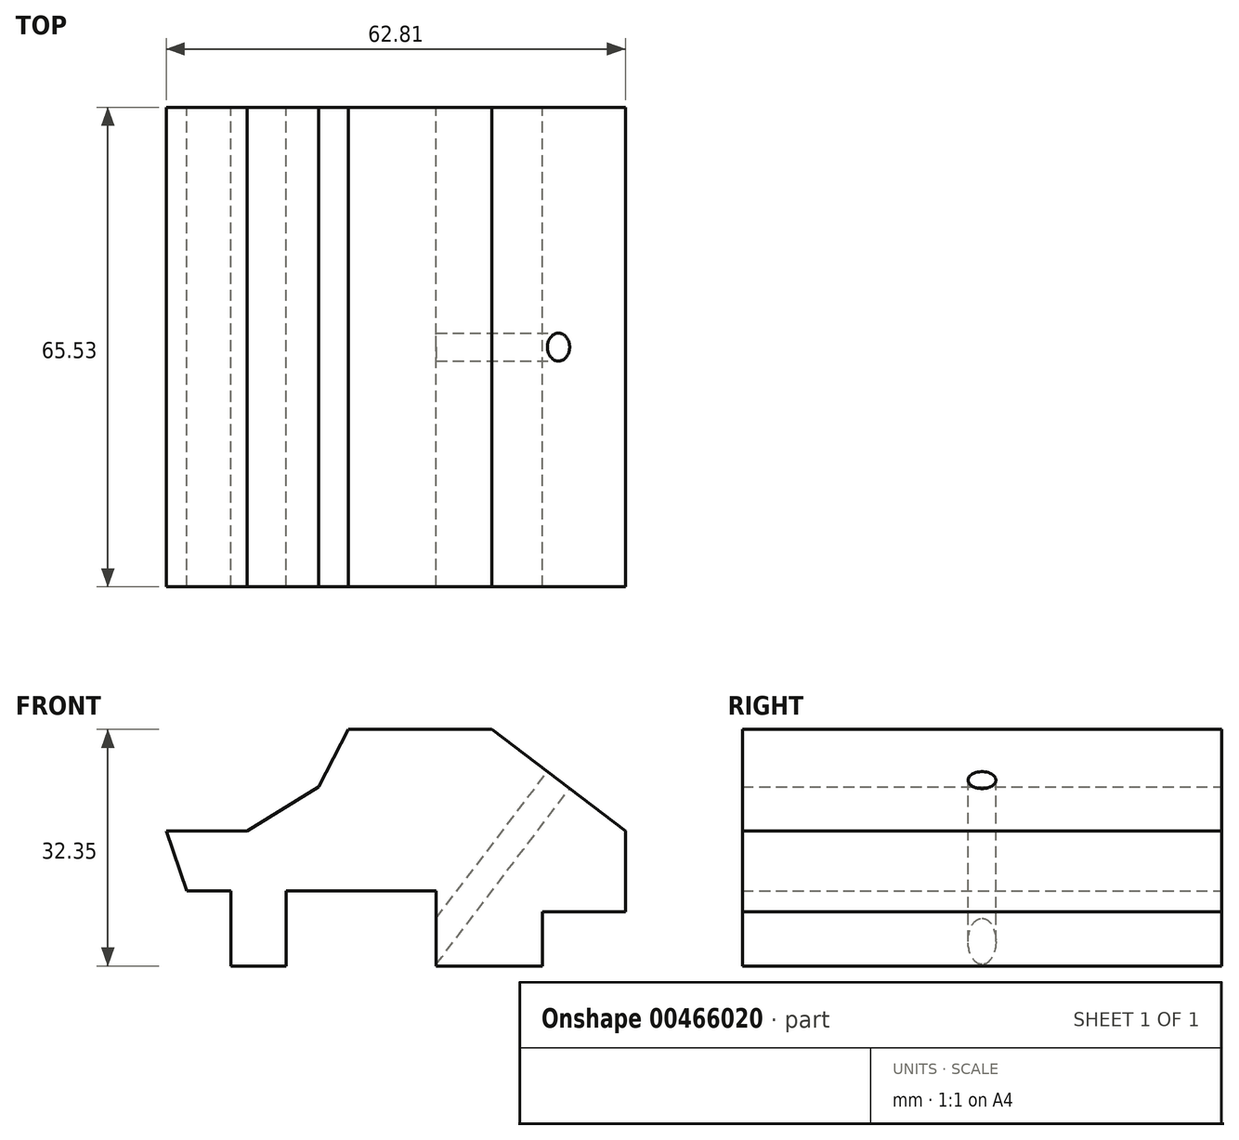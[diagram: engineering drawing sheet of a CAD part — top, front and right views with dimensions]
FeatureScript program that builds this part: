
annotation { "Feature Type Name" : "Feature", "Feature Type Description" : "" }
export const myFeature = defineFeature(function(context is Context, id is Id, definition is map)
    precondition{}
    {
        {
            var Q0;
            Q0=qCreatedBy(makeId("Front.planeOp"),FACE);
            var sketch = newSketch(context, id + "F0", { "sketchPlane" : qUnion([Q0])});
            skLineSegment(sketch, "E0", {"start": v(0, 0) * mm, "end": v(34.09, 0) * mm});
            skLineSegment(sketch, "E1", {"start": v(34.09, 0) * mm, "end": v(34.09, 10.26) * mm});
            skLineSegment(sketch, "E2", {"start": v(34.09, 10.26) * mm, "end": v(28.1, 10.26) * mm});
            skLineSegment(sketch, "E3", {"start": v(28.1, 10.26) * mm, "end": v(25.25, 18.46) * mm});
            skLineSegment(sketch, "E4", {"start": v(25.25, 18.46) * mm, "end": v(36.3, 18.46) * mm});
            skLineSegment(sketch, "E5", {"start": v(36.3, 18.46) * mm, "end": v(46.08, 24.46) * mm});
            skLineSegment(sketch, "E6", {"start": v(46.08, 24.46) * mm, "end": v(50.18, 32.35) * mm});
            skLineSegment(sketch, "E7", {"start": v(50.18, 32.35) * mm, "end": v(69.75, 32.35) * mm});
            skLineSegment(sketch, "E8", {"start": v(69.75, 32.35) * mm, "end": v(88.06, 18.46) * mm});
            skLineSegment(sketch, "E9", {"start": v(88.06, 18.46) * mm, "end": v(88.06, 7.42) * mm});
            skLineSegment(sketch, "E10", {"start": v(88.06, 7.42) * mm, "end": v(76.7, 7.42) * mm});
            skLineSegment(sketch, "E11", {"start": v(76.7, 7.42) * mm, "end": v(76.7, 0) * mm});
            skLineSegment(sketch, "E12", {"start": v(76.7, 0) * mm, "end": v(62.18, 0) * mm});
            skLineSegment(sketch, "E13", {"start": v(62.18, 0) * mm, "end": v(62.18, 10.26) * mm});
            skLineSegment(sketch, "E14", {"start": v(62.18, 10.26) * mm, "end": v(41.66, 10.26) * mm});
            skPoint(sketch, "E14.endSnap0", {"position": v(31.09, 10.26) * mm});
            skLineSegment(sketch, "E15", {"start": v(41.66, 10.26) * mm, "end": v(41.66, 0) * mm});
            skLineSegment(sketch, "E16", {"start": v(41.66, 0) * mm, "end": v(34.09, 0) * mm});
            skSolve(sketch);
        }
        {
            var Q0;
            Q0 = qSketchRegion(id + "F0", true);
            extrude(context, id + "F1", {"entities" : qUnion([Q0]), "depth" : 65.53 * mm});
        }
        {
            var Q0;
            Q0=makeQuery(id+"F1.opExtrude","SWEPT_FACE",FACE,{"disambiguationData":[OSD([sQuery(id+"F0.wireOp",EDGE,"E8")])]});
            var sketch = newSketch(context, id + "F2", { "sketchPlane" : qUnion([Q0])});
            skCircle(sketch, "E17", {"center": v(47.5, -32.77) * mm, "radius": 1.9 * mm});
            skPoint(sketch, "E17.centerSnap0", {"position": v(47.5, 0) * mm});
            skPoint(sketch, "E17.centerSnap1", {"position": v(59, -32.77) * mm});
            skSolve(sketch);
        }
        {
            var Q0;
            Q0=makeQuery(id+"F2.imprint","IMPRINT",FACE,{"disambiguationData":[TD([[makeQuery(id+"F2.imprint","IMPRINT",EDGE,{"derivedFrom":sQuery(id+"F2.wireOp",EDGE,"E17")}),1.0]])]});
            var Q1;
            Q1=sQuery(id+"F2.wireOp",EDGE,"E17");
            extrude(context, id + "F3", {"entities" : qUnion([Q0]), "operationType" : NewBodyOperationType.REMOVE, "surfaceEntities" : qUnion([Q1]), "endBound" : BoundingType.THROUGH_ALL, "oppositeDirection" : true, "depth" : 25.4 * mm});
        }
    });
